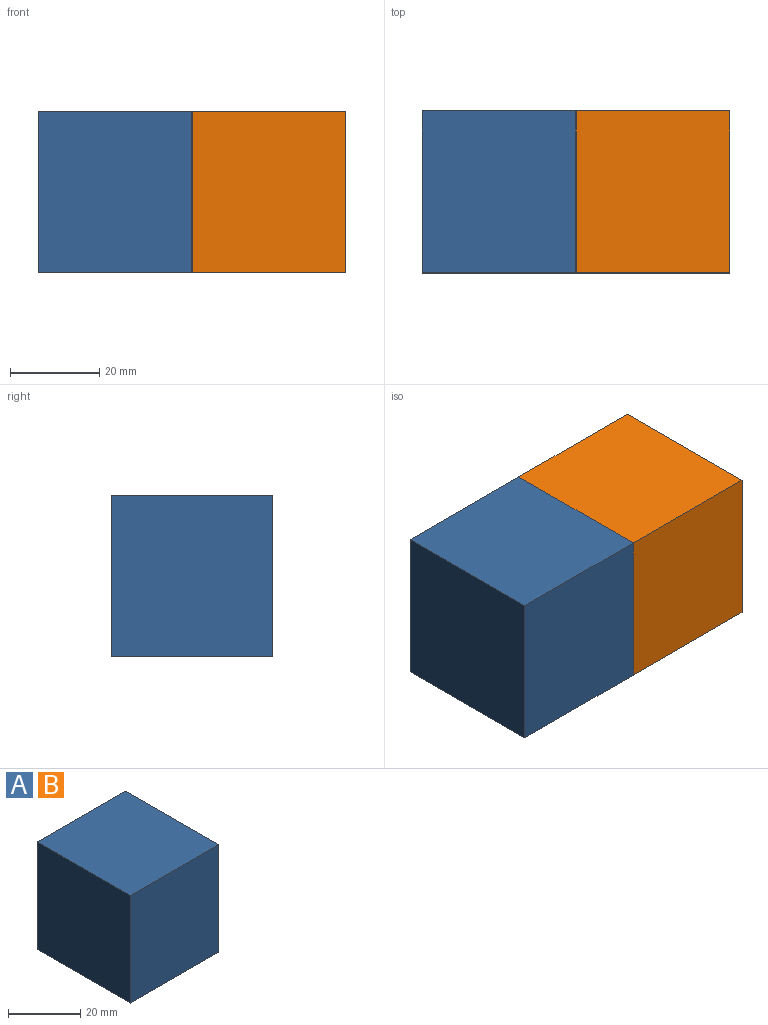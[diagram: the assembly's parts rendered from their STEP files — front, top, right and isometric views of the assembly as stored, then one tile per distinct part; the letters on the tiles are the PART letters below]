
ASSEMBLY  parts=2 mates=1
PART A: 6 faces, bbox 34.5x36.3x36.3 mm
  f0: plane 36.35x36.32mm, normal (-1,0,0), area 1320.2mm2, adj f1,f3,f4,f5
  f1: plane 36.32x34.52mm, normal (0,-1,0), area 1253.8mm2, adj f0,f2,f4,f5
  f2: plane 36.35x36.32mm, normal (1,0,0), area 1320.2mm2, adj f1,f3,f4,f5
  f3: plane 36.32x34.52mm, normal (0,1,0), area 1253.8mm2, adj f0,f2,f4,f5
  f4: plane 36.35x34.52mm, normal (0,0,1), area 1254.7mm2, adj f0,f1,f2,f3
  f5: plane 36.35x34.52mm, normal (0,0,-1), area 1254.7mm2, adj f0,f1,f2,f3
PART B: same geometry as A
PLACE A t=(-11.87,12.58,-17.59)mm
PLACE B t=(22.64,12.58,-17.59)mm
MATE fastened A.f2 <-> B.f0  axis (1,0,0) through (22.64,30.75,0.57)mm
